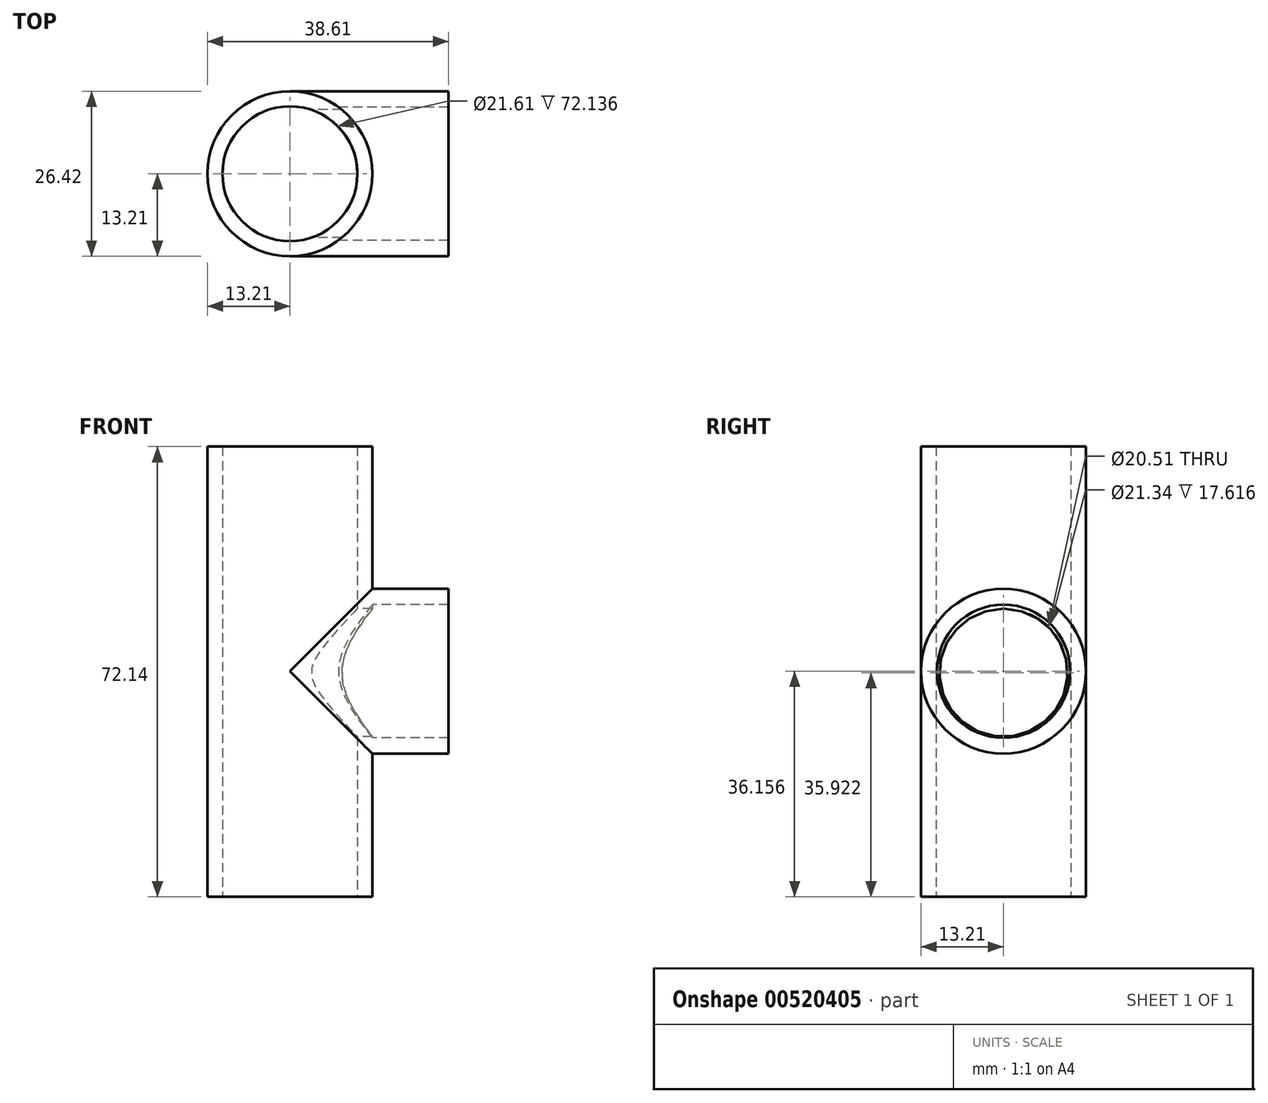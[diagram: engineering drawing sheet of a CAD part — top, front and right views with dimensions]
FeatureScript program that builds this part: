
annotation { "Feature Type Name" : "Feature", "Feature Type Description" : "" }
export const myFeature = defineFeature(function(context is Context, id is Id, definition is map)
    precondition{}
    {
        {
            var Q0;
            Q0=qCreatedBy(makeId("Top.planeOp"),FACE);
            var sketch = newSketch(context, id + "F0", { "sketchPlane" : qUnion([Q0])});
            skCircle(sketch, "E0", {"center": v(0, 0) * mm, "radius": 10.67 * mm});
            skCircle(sketch, "E1", {"center": v(0, 0) * mm, "radius": 13.2 * mm});
            skSolve(sketch);
        }
        {
            var Q0;
            Q0=makeQuery(id+"F0.imprint","IMPRINT",FACE,{"disambiguationData":[TD([[makeQuery(id+"F0.imprint","IMPRINT",EDGE,{"derivedFrom":sQuery(id+"F0.wireOp",EDGE,"E0")}),-1.0]])]});
            extrude(context, id + "F1", {"entities" : qUnion([Q0]), "depth" : 72.14 * mm, "offsetDistance" : 25.4 * mm});
        }
        {
            var Q0;
            Q0=qCreatedBy(makeId("Right.planeOp"),FACE);
            var sketch = newSketch(context, id + "F2", { "sketchPlane" : qUnion([Q0])});
            skCircle(sketch, "E2", {"center": v(0, 36.16) * mm, "radius": 10.67 * mm});
            skCircle(sketch, "E3", {"center": v(0, 36.16) * mm, "radius": 13.2 * mm});
            skSolve(sketch);
        }
        {
            var Q0;
            Q0=makeQuery(id+"F2.imprint","IMPRINT",FACE,{"disambiguationData":[TD([[makeQuery(id+"F2.imprint","IMPRINT",EDGE,{"derivedFrom":sQuery(id+"F2.wireOp",EDGE,"E2")}),-1.0]])]});
            extrude(context, id + "F3", {"entities" : qUnion([Q0]), "operationType" : NewBodyOperationType.ADD, "depth" : 25.4 * mm, "offsetDistance" : 25.4 * mm});
        }
        {
            var Q0;
            Q0=qCreatedBy(makeId("Right.planeOp"),FACE);
            var sketch = newSketch(context, id + "F4", { "sketchPlane" : qUnion([Q0])});
            skCircle(sketch, "E4", {"center": v(0, 35.92) * mm, "radius": 10.26 * mm});
            skSolve(sketch);
        }
        {
            var Q0;
            Q0=makeQuery(id+"F4.imprint","IMPRINT",FACE,{"disambiguationData":[TD([[makeQuery(id+"F4.imprint","IMPRINT",EDGE,{"derivedFrom":sQuery(id+"F4.wireOp",EDGE,"E4")}),1.0]])]});
            extrude(context, id + "F5", {"entities" : qUnion([Q0]), "operationType" : NewBodyOperationType.REMOVE, "depth" : 25.4 * mm, "offsetDistance" : 25.4 * mm});
        }
        {
            var Q0;
            Q0=qCreatedBy(makeId("Top.planeOp"),FACE);
            var sketch = newSketch(context, id + "F6", { "sketchPlane" : qUnion([Q0])});
            skCircle(sketch, "E5", {"center": v(0, 0) * mm, "radius": 10.8 * mm});
            skSolve(sketch);
        }
        {
            var Q0;
            Q0=makeQuery(id+"F6.imprint","IMPRINT",FACE,{"disambiguationData":[TD([[makeQuery(id+"F6.imprint","IMPRINT",EDGE,{"derivedFrom":sQuery(id+"F6.wireOp",EDGE,"E5")}),1.0]])]});
            extrude(context, id + "F7", {"entities" : qUnion([Q0]), "operationType" : NewBodyOperationType.REMOVE, "depth" : 76.2 * mm, "offsetDistance" : 25.4 * mm});
        }
    });
